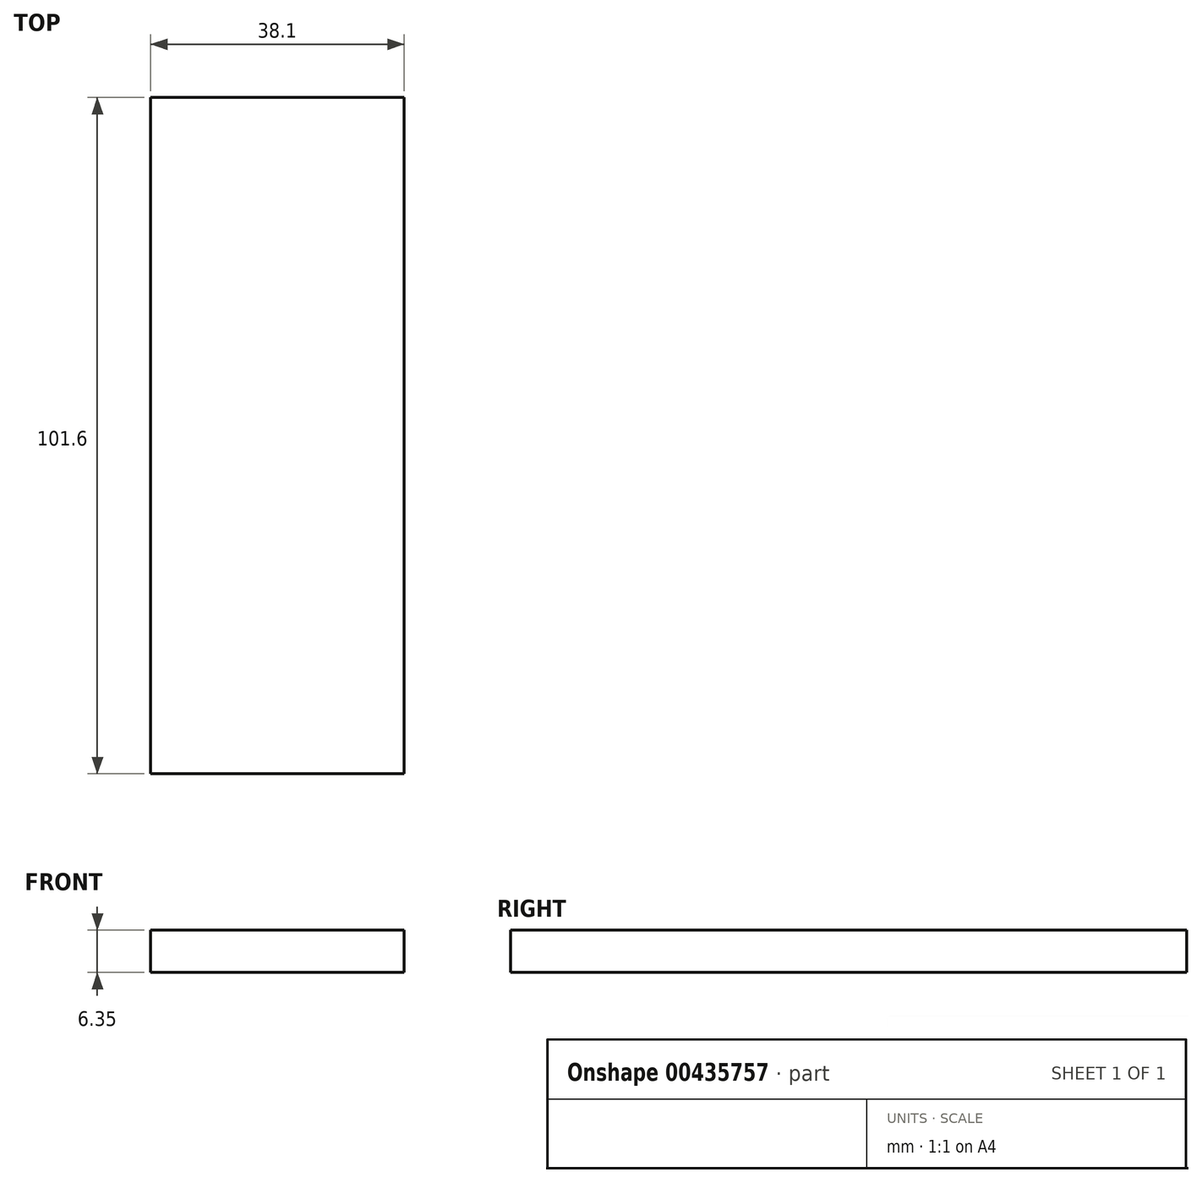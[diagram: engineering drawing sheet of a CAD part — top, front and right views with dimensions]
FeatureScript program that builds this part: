
annotation { "Feature Type Name" : "Feature", "Feature Type Description" : "" }
export const myFeature = defineFeature(function(context is Context, id is Id, definition is map)
    precondition{}
    {
        {
            var Q0;
            Q0=qCreatedBy(makeId("Top.planeOp"),FACE);
            var sketch = newSketch(context, id + "F0", { "sketchPlane" : qUnion([Q0])});
            skLineSegment(sketch, "E0.bottom", {"start": v(-19.05, 50.8) * mm, "end": v(19.05, 50.8) * mm});
            skLineSegment(sketch, "E0.top", {"start": v(-19.05, -50.8) * mm, "end": v(19.05, -50.8) * mm});
            skLineSegment(sketch, "E0.left", {"start": v(-19.05, 50.8) * mm, "end": v(-19.05, -50.8) * mm});
            skLineSegment(sketch, "E0.right", {"start": v(19.05, 50.8) * mm, "end": v(19.05, -50.8) * mm});
            skPoint(sketch, "E0.middle", {"position": v(0, 0) * mm});
            skSolve(sketch);
        }
        {
            var Q0;
            Q0=makeQuery(id+"F0.imprint","IMPRINT",FACE,{"disambiguationData":[TD([[makeQuery(id+"F0.imprint","IMPRINT",EDGE,{"derivedFrom":sQuery(id+"F0.wireOp",EDGE,"E0.bottom")}),-1.0]])]});
            extrude(context, id + "F1", {"entities" : qUnion([Q0]), "depth" : 6.35 * mm});
        }
    });
